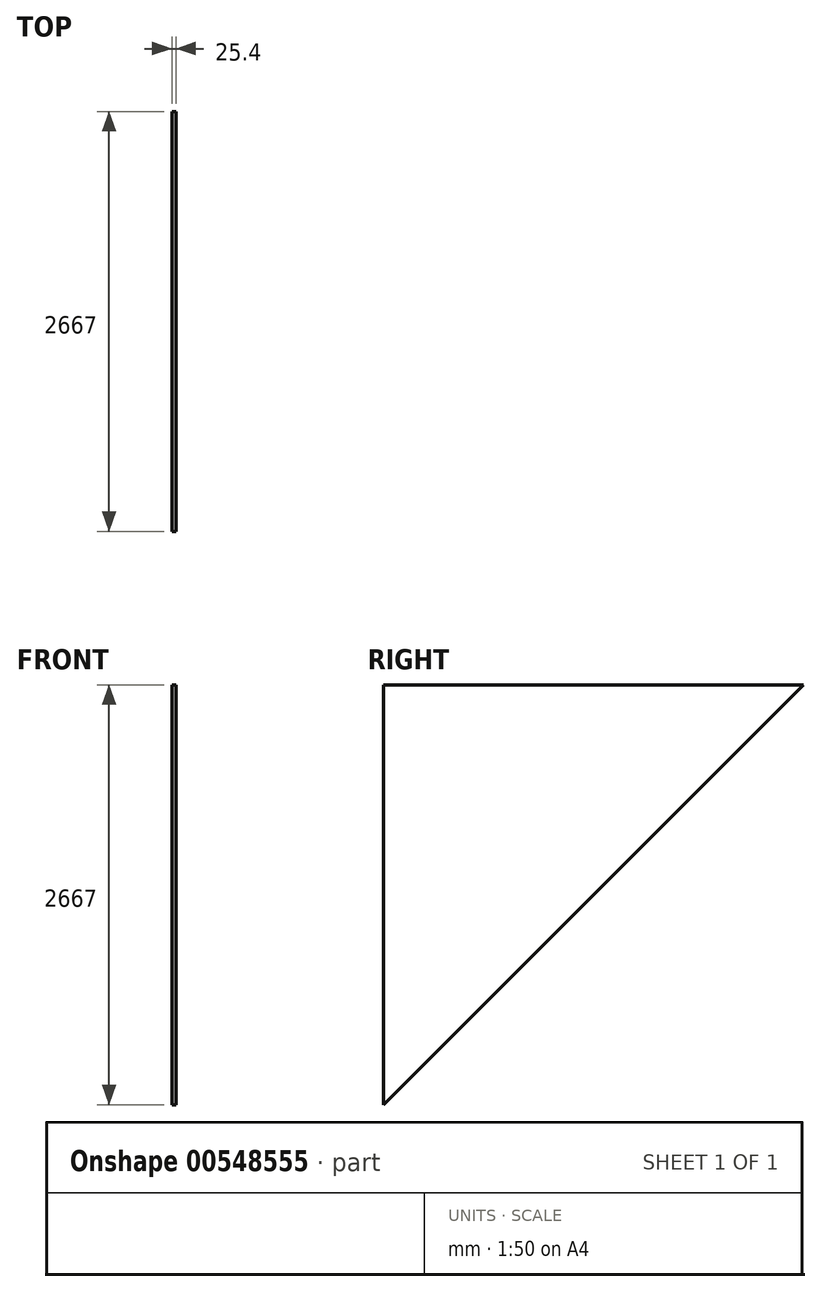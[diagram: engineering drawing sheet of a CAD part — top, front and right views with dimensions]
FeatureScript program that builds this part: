
annotation { "Feature Type Name" : "Feature", "Feature Type Description" : "" }
export const myFeature = defineFeature(function(context is Context, id is Id, definition is map)
    precondition{}
    {
        {
            var Q0;
            Q0=qCreatedBy(makeId("Right.planeOp"),FACE);
            var sketch = newSketch(context, id + "F0", { "sketchPlane" : qUnion([Q0])});
            skLineSegment(sketch, "E0", {"start": v(2667, 0) * mm, "end": v(0, 0) * mm});
            skLineSegment(sketch, "E1", {"start": v(0, 0) * mm, "end": v(0, -2667) * mm});
            skLineSegment(sketch, "E2", {"start": v(0, -2667) * mm, "end": v(2667, 0) * mm});
            skSolve(sketch);
        }
        {
            var Q0;
            Q0 = qSketchRegion(id + "F0", true);
            extrude(context, id + "F1", {"entities" : qUnion([Q0]), "depth" : 25.4 * mm, "offsetDistance" : 25.4 * mm});
        }
    });
